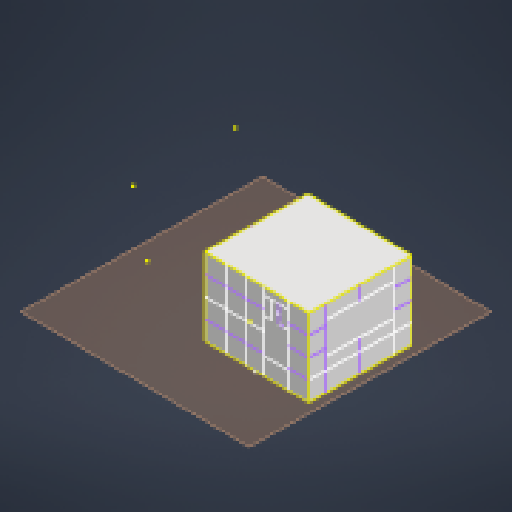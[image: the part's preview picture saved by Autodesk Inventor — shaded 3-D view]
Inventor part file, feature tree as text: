
AUTODESK INVENTOR PART (.ipt)
format: ipt  version: 2024 (Build 280153000, 153)  size: 204,288 bytes
history: native  units: mm
features: sketch x5, other x4, plane x1, extrude x1
ambient origin geometry x8: Origin, YZ Plane, XZ Plane, XY Plane, X Axis, Y Axis, Z Axis, Center Point
bodies: Body1 (feature_tree)
feature tree (11):
  other  "Sólido1"
  plane  "Plano de trabajo1"
  extrude  "Extrusión1"  Depth=2890.0mm
  sketch  "Boceto2"  dims[d2=2200.0mm d3=0.0mm]
  sketch  "Boceto3"  dims[d4=550.0mm d5=550.0mm]
  sketch  "Boceto4"  dims[d6=550.0mm]
  sketch  "Boceto5"  dims[d7=500.0mm d8=500.0mm d9=722.5mm d10=900.0mm d11=900.0mm d12=550.0mm d13=550.0mm d14=550.0mm d15=600.0mm d16=600.0mm d17=600.0mm d18=500.0mm d19=500.0mm d20=200.0mm d21=230.0mm d22=1000.0mm d23=205.0mm d24=600.0mm d25=600.0mm d26=500.0mm d27=600.0mm d28=550.0mm d29=550.0mm d30=550.0mm d31=500.0mm d33=205.0mm d34=230.0mm d35=200.0mm d36=1000.0mm d37=1800.0mm d38=800.0mm d39=800.0mm d40=500.0mm d41=500.0mm d42=500.0mm d43=500.0mm d44=200.0mm d45=200.0mm d46=495.0mm d47=1100.0mm]
  sketch  "Boceto1"  dims[d0=3000.0mm d1=2890.0mm]
  other  "<userpath>\Downloads\Celda_Robotizada.iam"
  other  "Celda_Robotizada.iam"
  other  "Piso:1"
